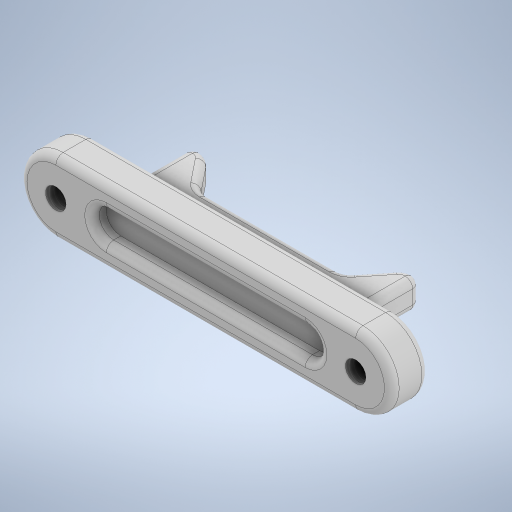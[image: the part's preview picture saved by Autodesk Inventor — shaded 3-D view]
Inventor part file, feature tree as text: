
AUTODESK INVENTOR PART (.ipt)
format: ipt  version: 2024 (Build 280153000, 153)  size: 380,928 bytes
history: native  units: in
note: dims shown in document units (in); Inventor stores cm internally (conversion verified against a paired STEP export)
features: sketch x4, extrude x3, fillet x2, other x2, hole x1, plane x1
ambient origin geometry x8: Origin, YZ Plane, XZ Plane, XY Plane, X Axis, Y Axis, Z Axis, Center Point
bodies: Solid1 (feature_tree)
feature tree (13):
  extrude  "Extrusion1"  Depth=0.315in
  extrude  "Extrusion2"  Depth=0.1625in TaperAngle=0.0deg
  hole  "Hole1"  [1 undecoded]
  plane  "Work Plane1"
  extrude  "Extrusion3"  Depth=0.275in
  fillet  "Fillet1"  [1 undecoded]
  fillet  "Fillet2"  Radius=0.0625in
  sketch  "Sketch1"  dims[d0=1.305in d1=0.315in]
  sketch  "Sketch2"  dims[d2=0.1575in d3=0.1625in d4=0.0in]
  sketch  "Sketch3"  dims[d5=0.865in d6=0.125in]
  other  "Work Axis1"
  other  "Work Axis2"
  sketch  "Sketch5"  dims[d7=0.0625in d8=0.0in d9=0.0894in d10=0.224in d11=0.375in d12=0.25in d13=0.5635in d14=1.0in d15=0.8108in d16=0.275in d17=180.0deg d18=0.0625in d19=0.625in d20=0.125in d21=0.315in d22=0.125in d23=0.0in d24=0.0625in d25=0.032in]
note: 2 required parameter values undecoded (feature->parameter linkage not recoverable at this tier; creation-order binding heuristic only, values carry confidence <= 0.55)
